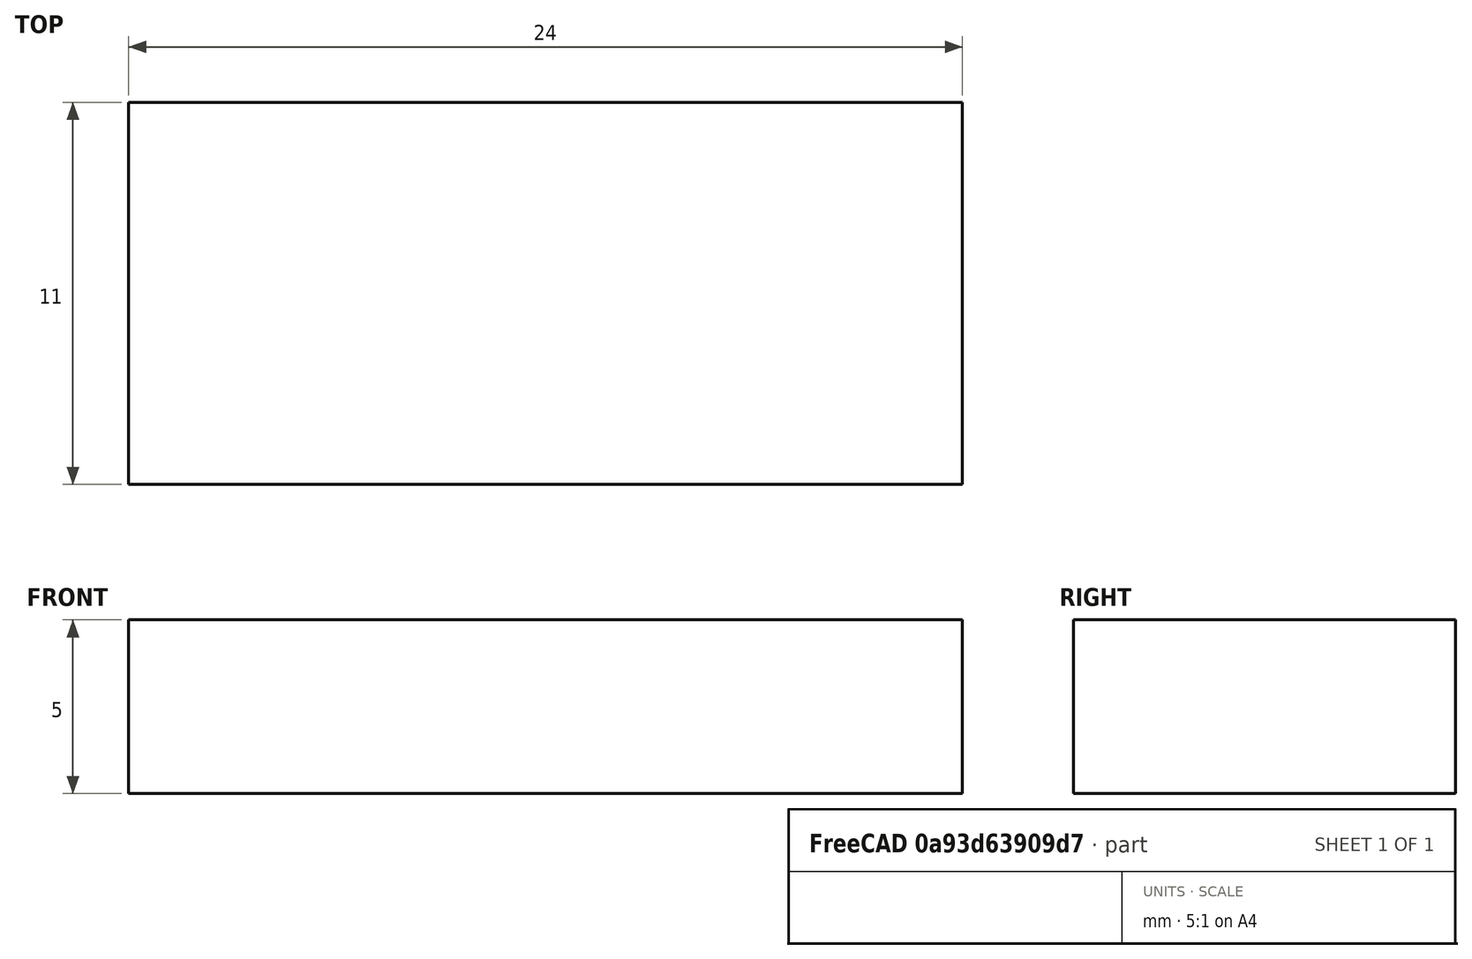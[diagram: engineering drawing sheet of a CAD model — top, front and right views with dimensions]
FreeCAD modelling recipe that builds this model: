
FCSTD DOCUMENT  (FreeCAD 0.19.4R1_voidlinux)
Label: back_lid_foam
License: All rights reserved
LicenseURL: http://en.wikipedia.org/wiki/All_rights_reserved
objects: Sketcher::SketchObject×1, PartDesign::Pad×1, PartDesign::CoordinateSystem×1, App::Part×1
note: 4 computed .brp shape members not serialized (recipe doc carries the construction recipe); baked Part::Feature solids carry a one-line shape summary decoded from their .brp
EXTERNAL_REF file=master_animator.FCStd obj=Variables

FEATURE [Sketcher::SketchObject] Sketch
  FullyConstrained = true
  MapMode = 5
  sketch-geometry (4):
    g0: LineSegment StartX=-12 StartY=0 StartZ=0 EndX=12 EndY=1.8e-15 EndZ=0
    g1: LineSegment StartX=12 StartY=1.8e-15 StartZ=0 EndX=12 EndY=11 EndZ=0
    g2: LineSegment StartX=12 StartY=11 StartZ=0 EndX=-12 EndY=11 EndZ=0
    g3: LineSegment StartX=-12 StartY=11 StartZ=0 EndX=-12 EndY=0 EndZ=0
  constraints (11):
    c: Coincident(g0,g1)
    c: Coincident(g1,g2)
    c: Coincident(g2,g3)
    c: Coincident(g3,g0)
    c: Horizontal(g2)
    c: Vertical(g1)
    c: Vertical(g3)
    c: PointOnObject(g0,g-1)
    c: Symmetric(g0,g0,g-2)
    c: Distance(g2,g1) = 24
    c: Distance(g1,g0) = 11
FEATURE [PartDesign::Pad] Pad
  Direction = (1,1,1)
  Length = 5
  Length2 = 100
  Profile = -> Sketch
  Type = 0
FEATURE [PartDesign::CoordinateSystem] foam_back_center
  AttacherType = Attacher::AttachEngine3D
  MapMode = 45
  Placement = pos=(-4e-16,5.5,0) rot=(0,0,1;1.5708rad)
  Support = -> [Pad]
  expr: .AttachmentOffset.Base.z = -master_animator#Variables.explode * 3
FEATURE [App::Part] Part  label="back_lid_foam"
  Group = -> [Pad,Sketch,foam_back_center]
  Origin = -> Origin
